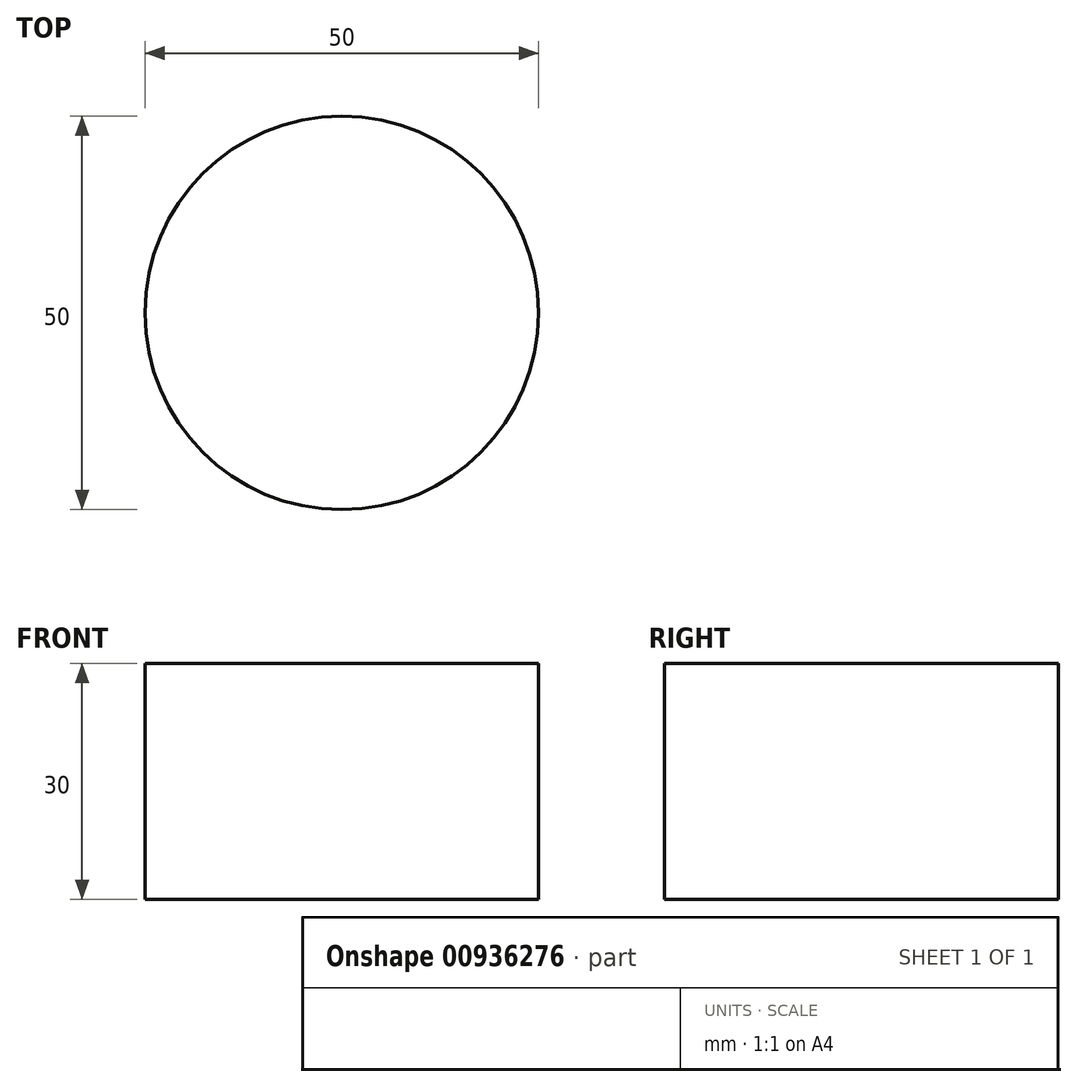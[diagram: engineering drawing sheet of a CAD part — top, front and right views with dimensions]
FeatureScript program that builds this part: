
annotation { "Feature Type Name" : "Feature", "Feature Type Description" : "" }
export const myFeature = defineFeature(function(context is Context, id is Id, definition is map)
    precondition{}
    {
        {
            var Q0;
            Q0=qCreatedBy(makeId("Top.planeOp"),FACE);
            var sketch = newSketch(context, id + "F0", { "sketchPlane" : qUnion([Q0])});
            skCircle(sketch, "E0", {"center": v(0, 0) * mm, "radius": 25 * mm});
            skSolve(sketch);
        }
        {
            var Q0;
            Q0=makeQuery(id+"F0.imprint","IMPRINT",FACE,{"disambiguationData":[TD([[makeQuery(id+"F0.imprint","IMPRINT",EDGE,{"derivedFrom":sQuery(id+"F0.wireOp",EDGE,"E0")}),1.0]])]});
            extrude(context, id + "F1", {"entities" : qUnion([Q0]), "depth" : 30 * mm, "offsetDistance" : 25 * mm});
        }
    });
